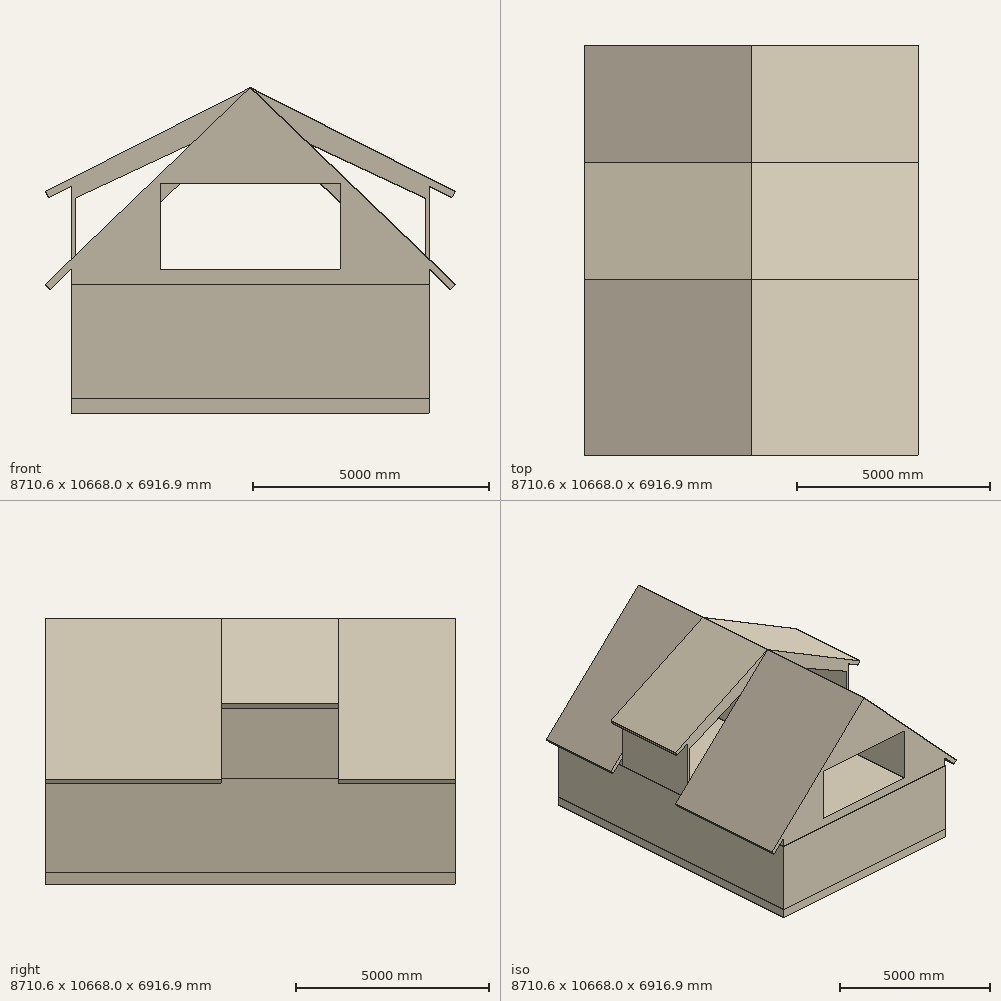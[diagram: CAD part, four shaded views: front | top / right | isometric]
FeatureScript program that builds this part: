
annotation { "Feature Type Name" : "Feature", "Feature Type Description" : "" }
export const myFeature = defineFeature(function(context is Context, id is Id, definition is map)
    precondition{}
    {
        {
            var Q0;
            Q0=qCreatedBy(makeId("Top.planeOp"),FACE);
            var sketch = newSketch(context, id + "F0", { "sketchPlane" : qUnion([Q0])});
            skLineSegment(sketch, "E0.bottom", {"start": v(0, 0) * mm, "end": v(7620, 0) * mm});
            skLineSegment(sketch, "E0.top", {"start": v(0, 10668) * mm, "end": v(7620, 10668) * mm});
            skLineSegment(sketch, "E0.left", {"start": v(0, 0) * mm, "end": v(0, 10668) * mm});
            skLineSegment(sketch, "E0.right", {"start": v(7620, 0) * mm, "end": v(7620, 10668) * mm});
            skSolve(sketch);
        }
        {
            var Q0;
            Q0 = qSketchRegion(id + "F0", true);
            extrude(context, id + "F1", {"entities" : qUnion([Q0]), "depth" : 304.8 * mm});
        }
        {
            var Q0;
            Q0=makeQuery(id+"F1.opExtrude","CAP_FACE",FACE,{"disambiguationData":[OSD([sQuery(id+"F0.wireOp",EDGE,"E0.bottom"),sQuery(id+"F0.wireOp",EDGE,"E0.top"),sQuery(id+"F0.wireOp",EDGE,"E0.left"),sQuery(id+"F0.wireOp",EDGE,"E0.right")])],"isStart":false});
            var sketch = newSketch(context, id + "F2", { "sketchPlane" : qUnion([Q0])});
            skLineSegment(sketch, "E1.bottom", {"start": v(101.6, 10566.4) * mm, "end": v(7518.4, 10566.4) * mm});
            skLineSegment(sketch, "E1.top", {"start": v(101.6, 101.6) * mm, "end": v(7518.4, 101.6) * mm});
            skLineSegment(sketch, "E1.left", {"start": v(101.6, 10566.4) * mm, "end": v(101.6, 101.6) * mm});
            skLineSegment(sketch, "E1.right", {"start": v(7518.4, 10566.4) * mm, "end": v(7518.4, 101.6) * mm});
            skSolve(sketch);
        }
        {
            var Q0;
            Q0=makeQuery(id+"F2.imprint","IMPRINT",FACE,{"disambiguationData":[TD([[makeQuery(id+"F2.imprint","IMPRINT",EDGE,{"derivedFrom":sQuery(id+"F2.wireOp",EDGE,"E1.bottom")}),1.0]])]});
            extrude(context, id + "F3", {"entities" : qUnion([Q0]), "depth" : 2438.4 * mm});
        }
        {
            var Q0;
            Q0=makeQuery(id+"F3.opExtrude","SWEPT_FACE",FACE,{"disambiguationData":[OSD([sQuery(id+"F0.wireOp",EDGE,"E0.bottom")])]});
            cPlane(context, id + "F4", {"entities" : qUnion([Q0]), "cplaneType" : CPlaneType.OFFSET, "offset" : 7620 * mm, "oppositeDirection" : true, "width" : 152.4 * mm, "height" : 152.4 * mm});
        }
        {
            var Q0;
            Q0=makeQuery(id+"F3.opExtrude","SWEPT_FACE",FACE,{"disambiguationData":[OSD([sQuery(id+"F0.wireOp",EDGE,"E0.bottom")])]});
            cPlane(context, id + "F5", {"entities" : qUnion([Q0]), "cplaneType" : CPlaneType.OFFSET, "offset" : 4572 * mm, "oppositeDirection" : true, "width" : 152.4 * mm, "height" : 152.4 * mm});
        }
        {
            var Q0;
            Q0=makeQuery(id+"F3.opExtrude","SWEPT_FACE",FACE,{"disambiguationData":[OSD([sQuery(id+"F0.wireOp",EDGE,"E0.bottom")])]});
            cPlane(context, id + "F6", {"entities" : qUnion([Q0]), "cplaneType" : CPlaneType.OFFSET, "offset" : 12.7 * mm, "oppositeDirection" : true, "width" : 152.4 * mm, "height" : 152.4 * mm});
        }
        {
            var Q0;
            Q0=qCreatedBy(id+"F6.planeOp",FACE);
            var sketch = newSketch(context, id + "F7", { "sketchPlane" : qUnion([Q0])});
            skLineSegment(sketch, "E2", {"start": v(0, 2743.2) * mm, "end": v(0, 3048) * mm});
            skLineSegment(sketch, "E3", {"start": v(0, 3048) * mm, "end": v(-439.76, 2625.83) * mm});
            skLineSegment(sketch, "E4", {"start": v(-439.76, 2625.83) * mm, "end": v(-545.3, 2735.77) * mm});
            skLineSegment(sketch, "E5", {"start": v(-545.3, 2735.77) * mm, "end": v(3810, 6916.86) * mm});
            skLineSegment(sketch, "E6", {"start": v(3810, 6916.86) * mm, "end": v(8165.3, 2735.77) * mm});
            skLineSegment(sketch, "E7", {"start": v(8165.3, 2735.77) * mm, "end": v(8059.76, 2625.83) * mm});
            skLineSegment(sketch, "E8", {"start": v(8059.76, 2625.83) * mm, "end": v(7620, 3048) * mm});
            skLineSegment(sketch, "E9", {"start": v(7620, 3048) * mm, "end": v(7620, 2743.2) * mm});
            skLineSegment(sketch, "E10.bottom", {"start": v(1905, 4876.8) * mm, "end": v(5715, 4876.8) * mm});
            skLineSegment(sketch, "E10.top", {"start": v(1905, 3048) * mm, "end": v(5715, 3048) * mm});
            skLineSegment(sketch, "E10.left", {"start": v(1905, 4876.8) * mm, "end": v(1905, 3048) * mm});
            skLineSegment(sketch, "E10.right", {"start": v(5715, 4876.8) * mm, "end": v(5715, 3048) * mm});
            skLineSegment(sketch, "E11", {"start": v(3810, 6916.86) * mm, "end": v(3810, -3163.6) * mm, "construction": true});
            skLineSegment(sketch, "E12.0", {"start": v(0, 2743.2) * mm, "end": v(7620, 2743.2) * mm});
            skSolve(sketch);
        }
        {
            var Q0;
            Q0 = qSketchRegion(id + "F7", true);
            var Q1;
            Q1=qCreatedBy(id+"F5.planeOp",FACE);
            extrude(context, id + "F8", {"entities" : qUnion([Q0]), "endBound" : BoundingType.UP_TO_SURFACE, "oppositeDirection" : true, "endBoundEntityFace" : qUnion([Q1]), "depth" : 3048 * mm});
        }
        {
            var Q0;
            Q0=qCreatedBy(id+"F5.planeOp",FACE);
            var sketch = newSketch(context, id + "F9", { "sketchPlane" : qUnion([Q0])});
            skLineSegment(sketch, "E13.0.0", {"start": v(0, 3048) * mm, "end": v(-439.76, 2625.83) * mm, "construction": true});
            skLineSegment(sketch, "E13.0.1", {"start": v(-439.76, 2625.83) * mm, "end": v(-545.3, 2735.77) * mm, "construction": true});
            skLineSegment(sketch, "E13.0.2", {"start": v(-545.3, 2735.77) * mm, "end": v(3810, 6916.86) * mm, "construction": true});
            skLineSegment(sketch, "E13.0.3", {"start": v(3810, 6916.86) * mm, "end": v(8165.3, 2735.77) * mm, "construction": true});
            skLineSegment(sketch, "E13.0.4", {"start": v(8165.3, 2735.77) * mm, "end": v(8059.76, 2625.83) * mm, "construction": true});
            skLineSegment(sketch, "E13.0.5", {"start": v(8059.76, 2625.83) * mm, "end": v(7620, 3048) * mm, "construction": true});
            skLineSegment(sketch, "E13.0.6", {"start": v(7620, 3048) * mm, "end": v(7620, 2743.2) * mm, "construction": true});
            skLineSegment(sketch, "E13.0.7", {"start": v(7620, 2743.2) * mm, "end": v(0, 2743.2) * mm, "construction": true});
            skLineSegment(sketch, "E13.0.8", {"start": v(0, 2743.2) * mm, "end": v(0, 3048) * mm, "construction": true});
            skLineSegment(sketch, "E14.bottom", {"start": v(7620, 2743.2) * mm, "end": v(7518.4, 2743.2) * mm});
            skLineSegment(sketch, "E14.top", {"start": v(7620, 4572) * mm, "end": v(7518.4, 4572) * mm});
            skLineSegment(sketch, "E14.left", {"start": v(7620, 2743.2) * mm, "end": v(7620, 4572) * mm});
            skLineSegment(sketch, "E14.right", {"start": v(7518.4, 2743.2) * mm, "end": v(7518.4, 4572) * mm});
            skLineSegment(sketch, "E15.bottom", {"start": v(0, 2743.2) * mm, "end": v(101.6, 2743.2) * mm});
            skLineSegment(sketch, "E15.top", {"start": v(0, 4572) * mm, "end": v(101.6, 4572) * mm});
            skLineSegment(sketch, "E15.left", {"start": v(0, 2743.2) * mm, "end": v(0, 4572) * mm});
            skLineSegment(sketch, "E15.right", {"start": v(101.6, 2743.2) * mm, "end": v(101.6, 4572) * mm});
            skLineSegment(sketch, "E16", {"start": v(3810, 6916.86) * mm, "end": v(-545.3, 4707.92) * mm});
            skLineSegment(sketch, "E17", {"start": v(-545.3, 4707.92) * mm, "end": v(-476.36, 4572) * mm});
            skLineSegment(sketch, "E18", {"start": v(-476.36, 4572) * mm, "end": v(0, 4813.6) * mm});
            skLineSegment(sketch, "E19", {"start": v(0, 4572) * mm, "end": v(0, 4813.6) * mm});
            skLineSegment(sketch, "E20", {"start": v(101.6, 4572) * mm, "end": v(3810, 6307.26) * mm});
            skLineSegment(sketch, "E21", {"start": v(3810, 6307.26) * mm, "end": v(7518.4, 4572) * mm});
            skLineSegment(sketch, "E22", {"start": v(7620, 4572) * mm, "end": v(7620, 4813.6) * mm});
            skLineSegment(sketch, "E23", {"start": v(7620, 4813.6) * mm, "end": v(8096.36, 4572) * mm});
            skLineSegment(sketch, "E24", {"start": v(8096.36, 4572) * mm, "end": v(8165.3, 4707.92) * mm});
            skLineSegment(sketch, "E25", {"start": v(8165.3, 4707.92) * mm, "end": v(3810, 6916.86) * mm});
            skSolve(sketch);
        }
        {
            var Q0;
            Q0=qCreatedBy(id+"F4.planeOp",FACE);
            var sketch = newSketch(context, id + "F10", { "sketchPlane" : qUnion([Q0])});
            skLineSegment(sketch, "E26.0.0", {"start": v(0, 3048) * mm, "end": v(0, 2743.2) * mm});
            skLineSegment(sketch, "E26.0.2", {"start": v(7620, 2743.2) * mm, "end": v(7620, 3048) * mm});
            skLineSegment(sketch, "E26.0.3", {"start": v(7620, 3048) * mm, "end": v(8059.76, 2625.83) * mm});
            skLineSegment(sketch, "E26.0.4", {"start": v(8059.76, 2625.83) * mm, "end": v(8165.3, 2735.77) * mm});
            skLineSegment(sketch, "E26.0.5", {"start": v(8165.3, 2735.77) * mm, "end": v(3810, 6916.86) * mm});
            skLineSegment(sketch, "E26.0.6", {"start": v(3810, 6916.86) * mm, "end": v(-545.3, 2735.77) * mm});
            skLineSegment(sketch, "E26.0.7", {"start": v(-545.3, 2735.77) * mm, "end": v(-439.76, 2625.83) * mm});
            skLineSegment(sketch, "E26.0.8", {"start": v(-439.76, 2625.83) * mm, "end": v(0, 3048) * mm});
            skLineSegment(sketch, "E27", {"start": v(3810, 6307.26) * mm, "end": v(7518.4, 2743.2) * mm});
            skLineSegment(sketch, "E28", {"start": v(3810, 6307.26) * mm, "end": v(101.6, 2743.2) * mm});
            skLineSegment(sketch, "E29", {"start": v(0, 2743.2) * mm, "end": v(101.6, 2743.2) * mm});
            skLineSegment(sketch, "E30", {"start": v(7518.4, 2743.2) * mm, "end": v(7620, 2743.2) * mm});
            skSolve(sketch);
        }
        {
            var Q0;
            Q0 = qSketchRegion(id + "F10", true);
            var Q1;
            Q1=makeQuery(id+"F3.opExtrude","SWEPT_FACE",FACE,{"disambiguationData":[OSD([sQuery(id+"F0.wireOp",EDGE,"E0.top")])]});
            extrude(context, id + "F11", {"entities" : qUnion([Q0]), "endBound" : BoundingType.UP_TO_SURFACE, "oppositeDirection" : true, "endBoundEntityFace" : qUnion([Q1]), "depth" : 25.4 * mm});
        }
        {
            var Q0;
            Q0 = qSketchRegion(id + "F9", true);
            var Q1;
            Q1=qCreatedBy(id+"F4.planeOp",FACE);
            extrude(context, id + "F12", {"entities" : qUnion([Q0]), "endBound" : BoundingType.UP_TO_SURFACE, "oppositeDirection" : true, "endBoundEntityFace" : qUnion([Q1]), "depth" : 25.4 * mm});
        }
        {
            var Q0;
            Q0=makeQuery(id+"F8.opExtrude","CAP_FACE",FACE,{"disambiguationData":[OSD([sQuery(id+"F7.wireOp",EDGE,"E2"),sQuery(id+"F7.wireOp",EDGE,"E3"),sQuery(id+"F7.wireOp",EDGE,"E4"),sQuery(id+"F7.wireOp",EDGE,"E5"),sQuery(id+"F7.wireOp",EDGE,"E6"),sQuery(id+"F7.wireOp",EDGE,"E7"),sQuery(id+"F7.wireOp",EDGE,"E8"),sQuery(id+"F7.wireOp",EDGE,"E9"),sQuery(id+"F7.wireOp",EDGE,"E10.bottom"),sQuery(id+"F7.wireOp",EDGE,"E10.top"),sQuery(id+"F7.wireOp",EDGE,"E10.left"),sQuery(id+"F7.wireOp",EDGE,"E10.right"),sQuery(id+"F7.wireOp",EDGE,"E12.0")])],"isStart":false});
            var sketch = newSketch(context, id + "F13", { "sketchPlane" : qUnion([Q0])});
            skLineSegment(sketch, "E31.bottom", {"start": v(-5715, 3048) * mm, "end": v(-2916.28, 3048) * mm});
            skLineSegment(sketch, "E31.top", {"start": v(-5715, 2743.2) * mm, "end": v(-2916.28, 2743.2) * mm});
            skLineSegment(sketch, "E31.left", {"start": v(-5715, 3048) * mm, "end": v(-5715, 2743.2) * mm});
            skLineSegment(sketch, "E31.right", {"start": v(-2916.28, 3048) * mm, "end": v(-2916.28, 2743.2) * mm});
            skSolve(sketch);
        }
        {
            var Q0;
            Q0 = qSketchRegion(id + "F13", true);
            extrude(context, id + "F14", {"entities" : qUnion([Q0]), "operationType" : NewBodyOperationType.ADD, "depth" : 1219.2 * mm});
        }
    });
